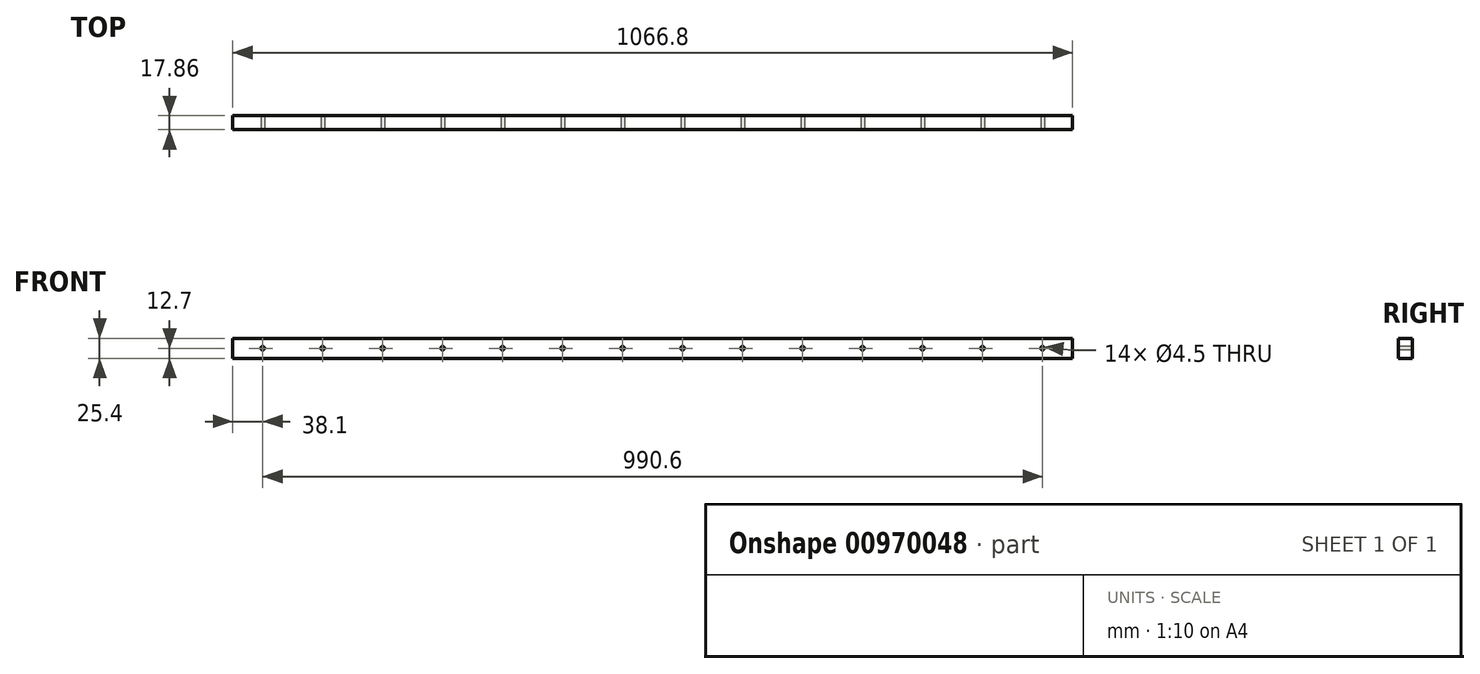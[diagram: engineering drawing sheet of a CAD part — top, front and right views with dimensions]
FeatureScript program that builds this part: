
annotation { "Feature Type Name" : "Feature", "Feature Type Description" : "" }
export const myFeature = defineFeature(function(context is Context, id is Id, definition is map)
    precondition{}
    {
        {
            var Q0;
            Q0=qCreatedBy(makeId("Right.planeOp"),FACE);
            var sketch = newSketch(context, id + "F0", { "sketchPlane" : qUnion([Q0])});
            skPoint(sketch, "E0.middle", {"position": v(0, 0) * mm});
            skLineSegment(sketch, "E1.bottom", {"start": v(0, 0) * mm, "end": v(-17.86, 0) * mm});
            skLineSegment(sketch, "E1.left", {"start": v(0, 0) * mm, "end": v(0, 25.4) * mm});
            skLineSegment(sketch, "E1.right", {"start": v(-17.86, 0) * mm, "end": v(-17.86, 25.4) * mm});
            skLineSegment(sketch, "E2", {"start": v(0, 25.4) * mm, "end": v(-17.86, 25.4) * mm});
            skSolve(sketch);
        }
        {
            var Q0;
            Q0=qSketchRegion(id+"F0",true);
            extrude(context, id + "F1", {"entities" : qUnion([Q0]), "depth" : 609.6 * mm, "offsetDistance" : 25.4 * mm, "hasSecondDirection" : true, "secondDirectionOppositeDirection" : true, "secondDirectionDepth" : 457.2 * mm});
        }
        {
            var Q0;
            Q0=makeQuery(id+"F1.opExtrude","SWEPT_FACE",FACE,{"disambiguationData":[OSD([sQuery(id+"F0.wireOp",EDGE,"E1.right")])]});
            var sketch = newSketch(context, id + "F2", { "sketchPlane" : qUnion([Q0])});
            skLineSegment(sketch, "E3", {"start": v(-457.2, 12.7) * mm, "end": v(609.6, 12.7) * mm, "construction": true});
            skPoint(sketch, "E4", {"position": v(38.1, 12.7) * mm});
            skPoint(sketch, "E5", {"position": v(114.3, 12.7) * mm});
            skPoint(sketch, "E6", {"position": v(190.5, 12.7) * mm});
            skPoint(sketch, "E7", {"position": v(266.7, 12.7) * mm});
            skPoint(sketch, "E8", {"position": v(342.9, 12.7) * mm});
            skPoint(sketch, "E9", {"position": v(419.1, 12.7) * mm});
            skPoint(sketch, "E10", {"position": v(495.3, 12.7) * mm});
            skPoint(sketch, "E11", {"position": v(571.5, 12.7) * mm});
            skPoint(sketch, "E12.MirrorP", {"position": v(-38.1, 12.7) * mm});
            skPoint(sketch, "E13.MirrorP", {"position": v(-114.3, 12.7) * mm});
            skPoint(sketch, "E14.MirrorP", {"position": v(-190.5, 12.7) * mm});
            skPoint(sketch, "E15.MirrorP", {"position": v(-266.7, 12.7) * mm});
            skPoint(sketch, "E16.MirrorP", {"position": v(-342.9, 12.7) * mm});
            skPoint(sketch, "E17.MirrorP", {"position": v(-419.1, 12.7) * mm});
            skSolve(sketch);
        }
        {
            var Q0;
            Q0=sQuery(id+"F2.wireOp",VERTEX,"E17.MirrorP");
            var Q1;
            Q1=sQuery(id+"F2.wireOp",VERTEX,"E16.MirrorP");
            var Q2;
            Q2=sQuery(id+"F2.wireOp",VERTEX,"E15.MirrorP");
            var Q3;
            Q3=sQuery(id+"F2.wireOp",VERTEX,"E14.MirrorP");
            var Q4;
            Q4=sQuery(id+"F2.wireOp",VERTEX,"E13.MirrorP");
            var Q5;
            Q5=sQuery(id+"F2.wireOp",VERTEX,"E12.MirrorP");
            var Q6;
            Q6=sQuery(id+"F2.wireOp",VERTEX,"E4");
            var Q7;
            Q7=sQuery(id+"F2.wireOp",VERTEX,"E5");
            var Q8;
            Q8=sQuery(id+"F2.wireOp",VERTEX,"E6");
            var Q9;
            Q9=sQuery(id+"F2.wireOp",VERTEX,"E7");
            var Q10;
            Q10=sQuery(id+"F2.wireOp",VERTEX,"E8");
            var Q11;
            Q11=sQuery(id+"F2.wireOp",VERTEX,"E9");
            var Q12;
            Q12=sQuery(id+"F2.wireOp",VERTEX,"E10");
            var Q13;
            Q13=sQuery(id+"F2.wireOp",VERTEX,"E11");
            var Q14;
            Q14=makeQuery(id+"F1.opExtrude","SWEPT_BODY",BODY,{"disambiguationData":[OSD([sQuery(id+"F0.wireOp",EDGE,"E1.bottom"),sQuery(id+"F0.wireOp",EDGE,"E1.left"),sQuery(id+"F0.wireOp",EDGE,"E1.right"),sQuery(id+"F0.wireOp",EDGE,"iVlerH18-5hcG-rphH-DsVK-T2HhoyOdLYZ7")])]});
            hole(context, id + "F3", {"style" : HoleStyle.SIMPLE, "endStyle" : HoleEndStyle.THROUGH, "standardTappedOrClearance" : lookupTablePath({ "standard" : "ANSI", "fit" : "Normal (ASME)", "size" : "#8", "type" : "Clearance" }), "standardBlindInLast" : lookupTablePath({ "fit" : "Free", "standard" : "ANSI", "size" : "#8", "type" : "Clearance" }), "holeDiameter" : 4.5 * mm, "majorDiameter" : 6.35 * mm, "isTappedThrough" : true, "tappedDepth" : 12.7 * mm, "tapClearance" : 3, "locations" : qUnion([Q0, Q1, Q2, Q3, Q4, Q5, Q6, Q7, Q8, Q9, Q10, Q11, Q12, Q13]), "scope" : qUnion([Q14])});
        }
    });
